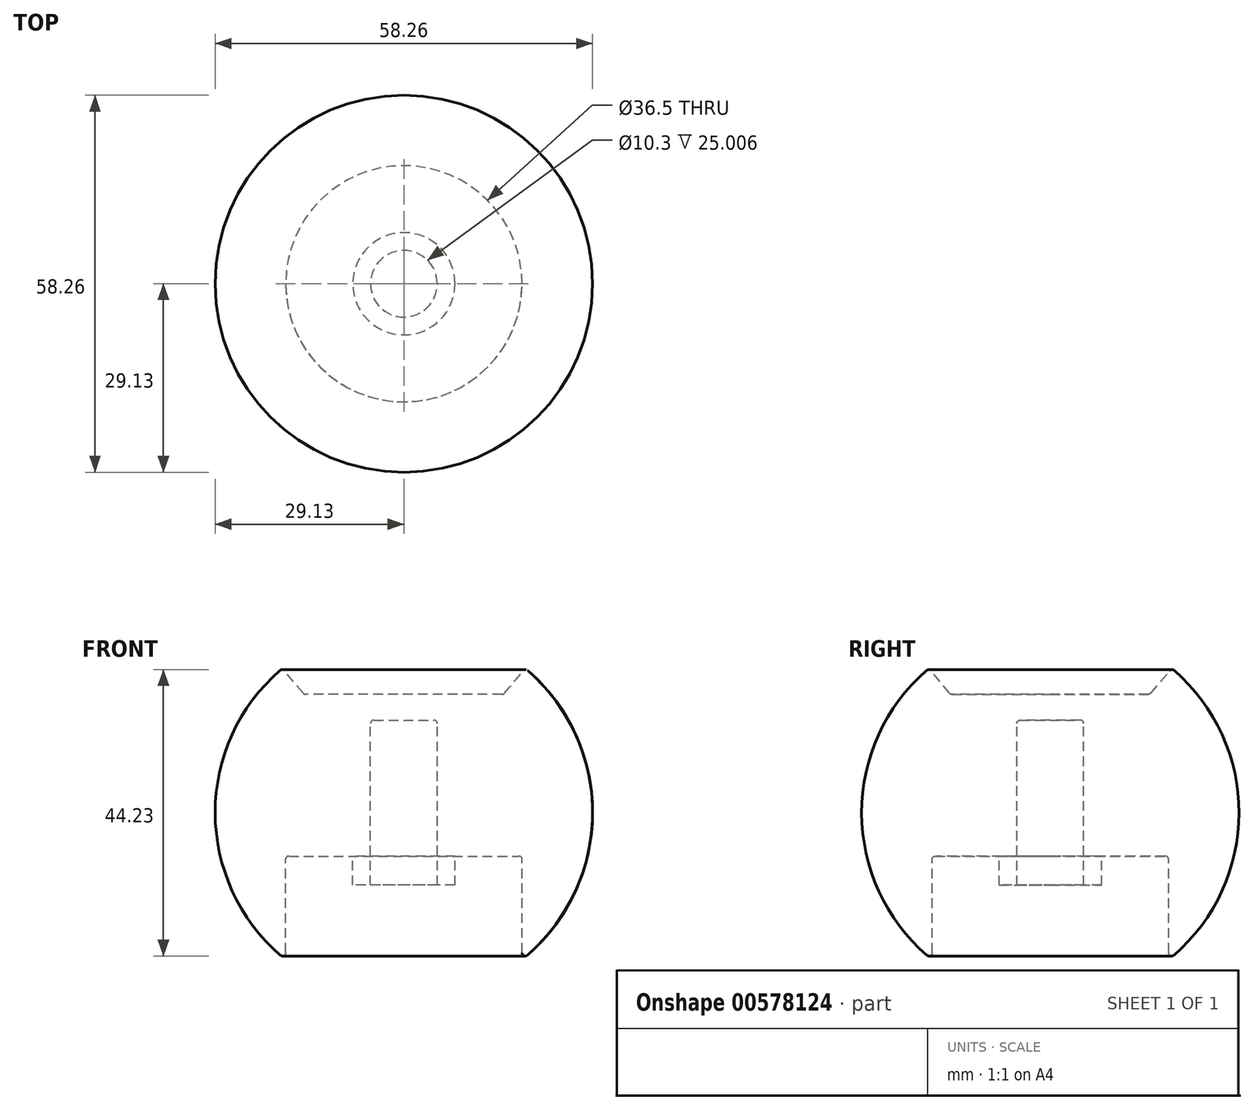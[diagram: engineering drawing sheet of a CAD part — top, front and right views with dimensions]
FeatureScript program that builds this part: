
annotation { "Feature Type Name" : "Feature", "Feature Type Description" : "" }
export const myFeature = defineFeature(function(context is Context, id is Id, definition is map)
    precondition{}
    {
        {
            var Q0;
            Q0=qCreatedBy(makeId("Front.planeOp"),FACE);
            var sketch = newSketch(context, id + "F0", { "sketchPlane" : qUnion([Q0])});
            skArc(sketch, "E0", {"start": v(-19.14, 21.96) * mm, "mid": v(-29.13, -0.04) * mm, "end": v(-19.08, -22.01) * mm});
            skLineSegment(sketch, "E1", {"start": v(0, 71.56) * mm, "end": v(0, -68.85) * mm, "construction": true});
            skLineSegment(sketch, "E2", {"start": v(0, 18.3) * mm, "end": v(-15.4, 18.3) * mm});
            skLineSegment(sketch, "E3", {"start": v(-15.4, 18.3) * mm, "end": v(-18.43, 21.9) * mm});
            skLineSegment(sketch, "E4", {"start": v(-18.25, -21.64) * mm, "end": v(-18.25, -6.7) * mm});
            skLineSegment(sketch, "E5", {"start": v(-5.15, -6.7) * mm, "end": v(-5.15, 14.3) * mm});
            skLineSegment(sketch, "E6", {"start": v(-5.15, 14.3) * mm, "end": v(0, 14.3) * mm});
            skLineSegment(sketch, "E7", {"start": v(0, 14.3) * mm, "end": v(0, 18.3) * mm});
            skPoint(sketch, "E8.orphan", {"position": v(-18.25, 14.31) * mm});
            skLineSegment(sketch, "E9", {"start": v(-18.75, 22.3) * mm, "end": v(-18.75, 33.13) * mm, "construction": true});
            skLineSegment(sketch, "E10", {"start": v(-18.25, -6.7) * mm, "end": v(-7.9, -6.7) * mm});
            skLineSegment(sketch, "E11", {"start": v(-7.9, -6.7) * mm, "end": v(-7.9, -11.2) * mm});
            skLineSegment(sketch, "E12", {"start": v(-7.9, -11.2) * mm, "end": v(-5.15, -11.2) * mm});
            skLineSegment(sketch, "E13", {"start": v(-5.15, -11.2) * mm, "end": v(-5.15, -6.7) * mm});
            skPoint(sketch, "E14.visualSharp", {"position": v(-18.25, -22.7) * mm});
            skArc(sketch, "E14.filletArc", {"start": v(-19.08, -22.01) * mm, "mid": v(-18.54, -22.1) * mm, "end": v(-18.25, -21.64) * mm});
            skPoint(sketch, "E15.visualSharp", {"position": v(-18.75, 22.3) * mm});
            skArc(sketch, "E15.filletArc", {"start": v(-18.43, 21.9) * mm, "mid": v(-18.77, 22.08) * mm, "end": v(-19.14, 21.96) * mm});
            skSolve(sketch);
        }
        {
            var Q0;
            Q0=makeQuery(id+"F0.imprint","IMPRINT",FACE,{"disambiguationData":[TD([[makeQuery(id+"F0.imprint","IMPRINT",EDGE,{"derivedFrom":sQuery(id+"F0.wireOp",EDGE,"E0")}),1.0]])]});
            var Q1;
            Q1=sQuery(id+"F0.wireOp",EDGE,"E1");
            revolve(context, id + "F1", {"entities" : qUnion([Q0]), "axis" : qUnion([Q1]), "revolveType" : RevolveType.FULL});
        }
        {
            var Q0;
            Q0=makeQuery(id+"F1.opRevolve","SWEPT_EDGE",EDGE,{"disambiguationData":[OSD([sQuery(id+"F0.wireOp",EDGE,"E5"),sQuery(id+"F0.wireOp",EDGE,"eIg05BSN-MFYB-GdZ7-BxfN-iD2ZUkaHKyjt")])]});
            var Q1;
            Q1=makeQuery(id+"F1.opRevolve","SWEPT_EDGE",EDGE,{"disambiguationData":[OSD([sQuery(id+"F0.wireOp",EDGE,"E0"),sQuery(id+"F0.wireOp",EDGE,"E4")])]});
            var Q2;
            Q2=makeQuery(id+"F1.opRevolve","SWEPT_EDGE",EDGE,{"disambiguationData":[OSD([sQuery(id+"F0.wireOp",EDGE,"E2"),sQuery(id+"F0.wireOp",EDGE,"E3")])]});
            var Q3;
            Q3=makeQuery(id+"F1.opRevolve","SWEPT_EDGE",EDGE,{"disambiguationData":[OSD([sQuery(id+"F0.wireOp",EDGE,"E0"),sQuery(id+"F0.wireOp",EDGE,"E3")])]});
            fillet(context, id + "F2", {"entities" : qUnion([Q0, Q1, Q2, Q3]), "radius" : 0.5 * mm, "tangentPropagation" : true, "allowEdgeOverflow" : false});
        }
    });
